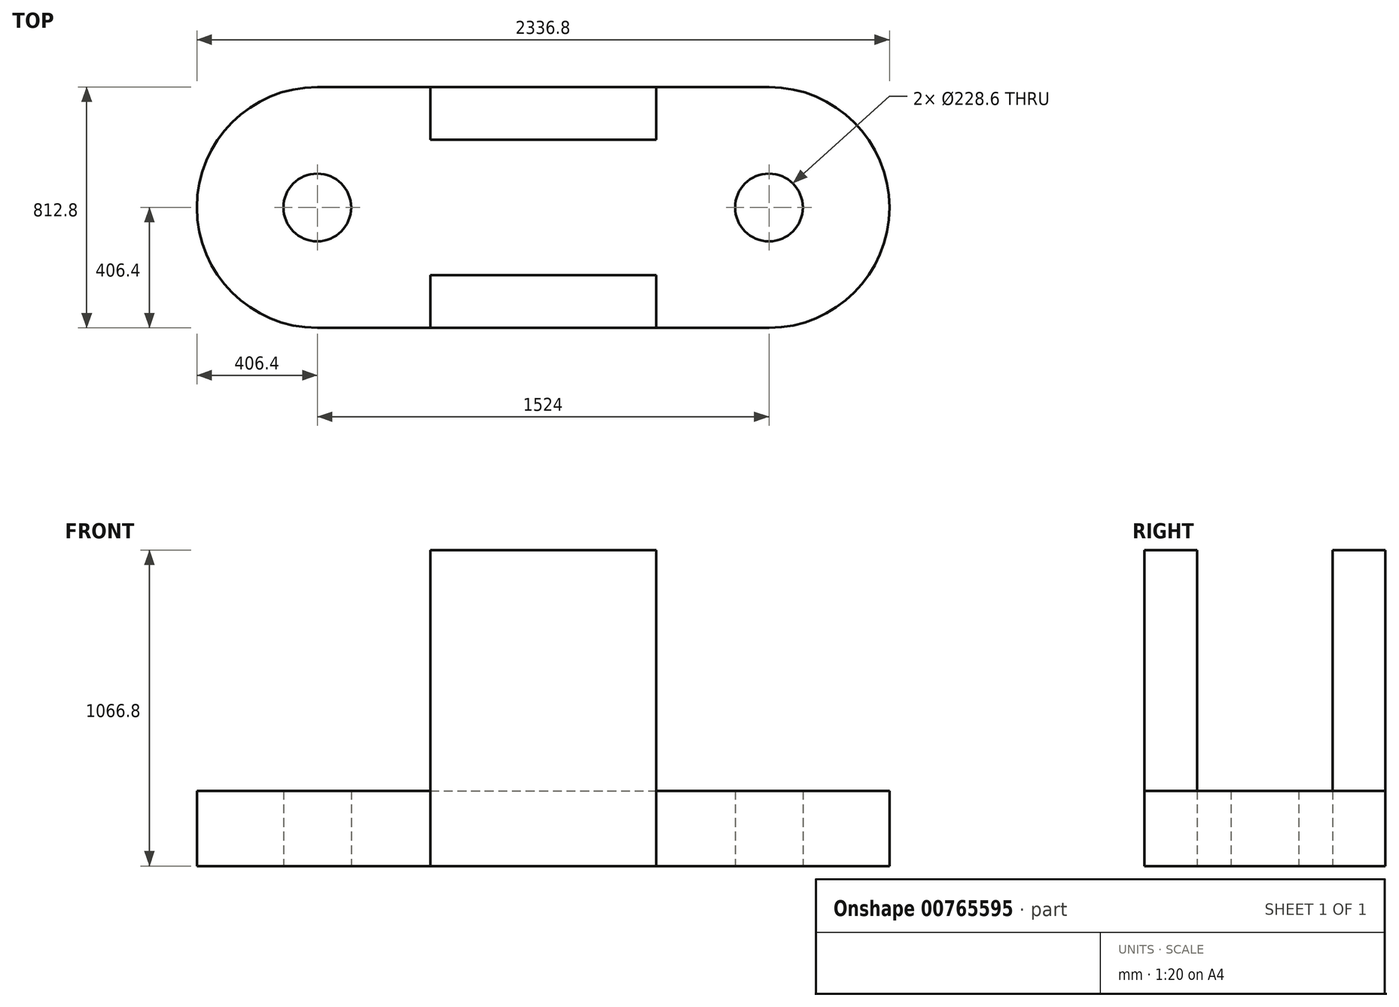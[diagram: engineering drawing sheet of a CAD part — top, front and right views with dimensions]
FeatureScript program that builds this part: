
annotation { "Feature Type Name" : "Feature", "Feature Type Description" : "" }
export const myFeature = defineFeature(function(context is Context, id is Id, definition is map)
    precondition{}
    {
        {
            var Q0;
            Q0=qCreatedBy(makeId("Top.planeOp"),FACE);
            var sketch = newSketch(context, id + "F0", { "sketchPlane" : qUnion([Q0])});
            skLineSegment(sketch, "E0.bottom", {"start": v(762, 406.4) * mm, "end": v(-762, 406.4) * mm});
            skLineSegment(sketch, "E0.top", {"start": v(762, -406.4) * mm, "end": v(-762, -406.4) * mm});
            skPoint(sketch, "E0.middle", {"position": v(0, 0) * mm});
            skCircle(sketch, "E1", {"center": v(-762, 0) * mm, "radius": 114.3 * mm});
            skCircle(sketch, "E2", {"center": v(762, 0) * mm, "radius": 114.3 * mm});
            skLineSegment(sketch, "E3.bottom", {"start": v(-381, -406.4) * mm, "end": v(381, -406.4) * mm});
            skLineSegment(sketch, "E3.top", {"start": v(-381, -228.6) * mm, "end": v(381, -228.6) * mm});
            skLineSegment(sketch, "E3.left", {"start": v(-381, -406.4) * mm, "end": v(-381, -228.6) * mm});
            skLineSegment(sketch, "E3.right", {"start": v(381, -406.4) * mm, "end": v(381, -228.6) * mm});
            skPoint(sketch, "E3.middle", {"position": v(0, -317.5) * mm});
            skLineSegment(sketch, "E4.bottom", {"start": v(-381, 406.4) * mm, "end": v(381, 406.4) * mm});
            skLineSegment(sketch, "E4.top", {"start": v(-381, 228.6) * mm, "end": v(381, 228.6) * mm});
            skLineSegment(sketch, "E4.left", {"start": v(-381, 406.4) * mm, "end": v(-381, 228.6) * mm});
            skLineSegment(sketch, "E4.right", {"start": v(381, 406.4) * mm, "end": v(381, 228.6) * mm});
            skPoint(sketch, "E4.middle", {"position": v(0, 317.5) * mm});
            skArc(sketch, "E5", {"start": v(-762, 406.4) * mm, "mid": v(-1168.4, 0) * mm, "end": v(-762, -406.4) * mm});
            skArc(sketch, "E6", {"start": v(762, -406.4) * mm, "mid": v(1168.4, 0) * mm, "end": v(762, 406.4) * mm});
            skSolve(sketch);
        }
        {
            var Q0;
            Q0=makeQuery(id+"F0.imprint","IMPRINT",FACE,{"disambiguationData":[TD([[makeQuery(id+"F0.imprint","IMPRINT",EDGE,{"derivedFrom":sQuery(id+"F0.wireOp",EDGE,"E3.top")}),-1.0]])]});
            extrude(context, id + "F1", {"entities" : qUnion([Q0]), "depth" : 1066.8 * mm, "offsetDistance" : 25.4 * mm});
        }
        {
            var Q0;
            Q0=makeQuery(id+"F0.imprint","IMPRINT",FACE,{"disambiguationData":[TD([[makeQuery(id+"F0.imprint","IMPRINT",EDGE,{"derivedFrom":sQuery(id+"F0.wireOp",EDGE,"E4.top")}),1.0]])]});
            extrude(context, id + "F2", {"entities" : qUnion([Q0]), "depth" : 1066.8 * mm, "offsetDistance" : 25.4 * mm});
        }
        {
            var Q0;
            Q0=makeQuery(id+"F0.imprint","IMPRINT",FACE,{"disambiguationData":[TD([[makeQuery(id+"F0.imprint","IMPRINT",EDGE,{"derivedFrom":sQuery(id+"F0.wireOp",EDGE,"E1")}),-1.0]])]});
            extrude(context, id + "F3", {"entities" : qUnion([Q0]), "depth" : 254 * mm, "offsetDistance" : 25.4 * mm});
        }
    });
